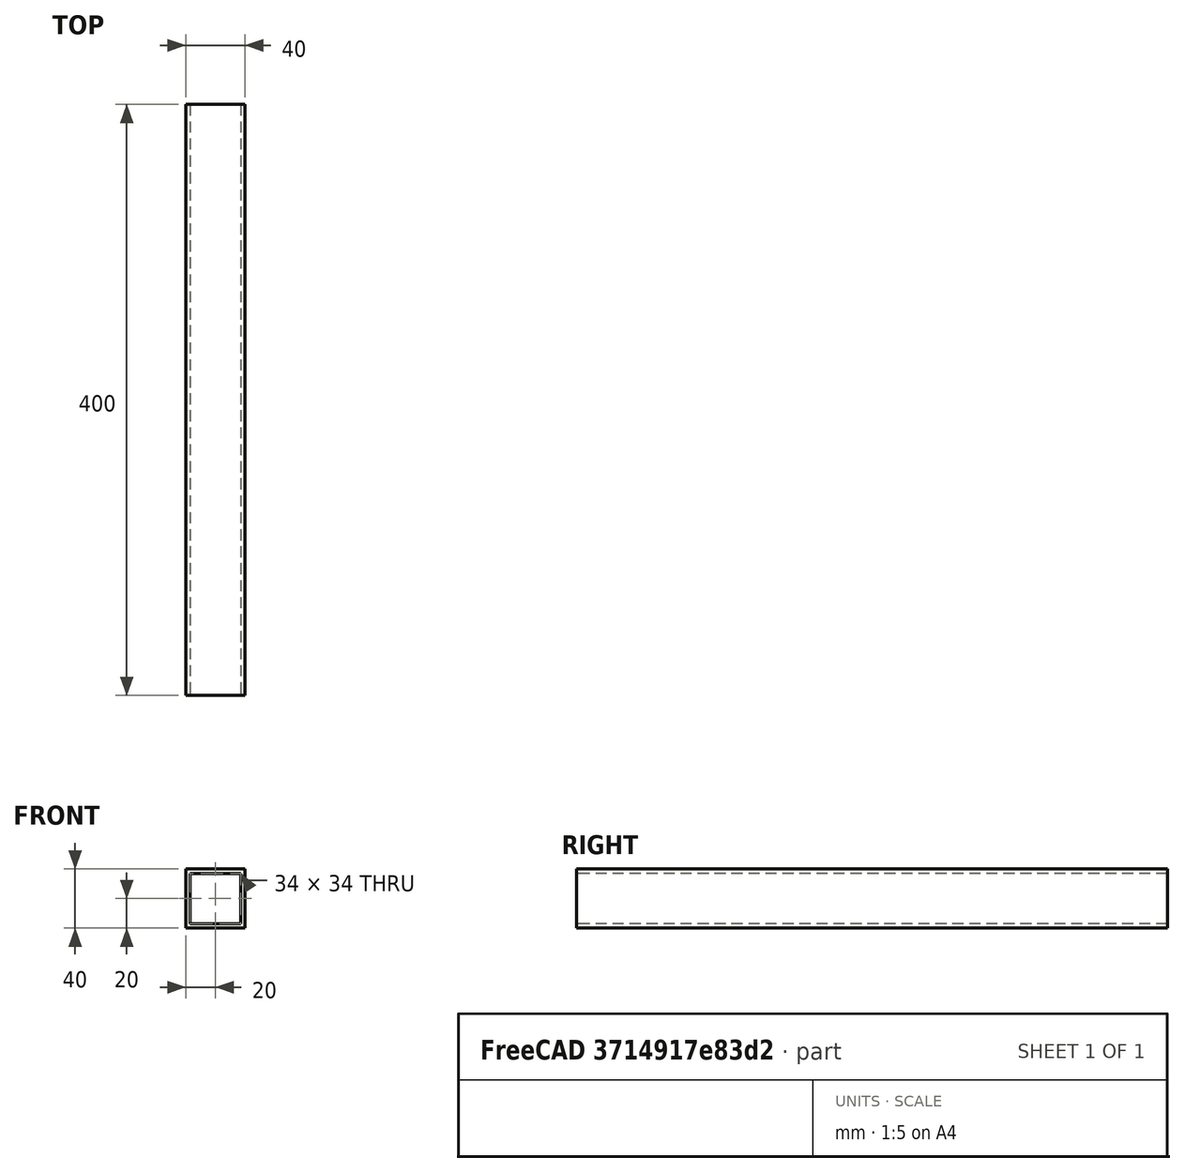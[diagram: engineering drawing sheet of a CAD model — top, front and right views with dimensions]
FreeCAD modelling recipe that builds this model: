
FCSTD DOCUMENT  (FreeCAD 0.20R29603 (Git))
Label: DaichselRohr
License: All rights reserved
LicenseURL: http://en.wikipedia.org/wiki/All_rights_reserved
objects: Sketcher::SketchObject×1, PartDesign::Pad×1, PartDesign::Body×1
note: 4 computed .brp shape members not serialized (recipe doc carries the construction recipe); baked Part::Feature solids carry a one-line shape summary decoded from their .brp

FEATURE [Sketcher::SketchObject] Sketch
  FullyConstrained = true
  MapMode = 5
  Placement = pos=(0,0,0) rot=(1,0,0;1.5708rad)
  Support = -> [XZ_Plane]
  sketch-geometry (10):
    g0: LineSegment StartX=-20 StartY=20 StartZ=0 EndX=-20 EndY=-20 EndZ=0
    g1: LineSegment StartX=-20 StartY=-20 StartZ=0 EndX=20 EndY=-20 EndZ=0
    g2: LineSegment StartX=20 StartY=-20 StartZ=0 EndX=20 EndY=20 EndZ=0
    g3: LineSegment StartX=20 StartY=20 StartZ=0 EndX=-20 EndY=20 EndZ=0
    g4: GeomPoint X=0 Y=0 Z=0
    g5: LineSegment StartX=-17 StartY=17 StartZ=0 EndX=-17 EndY=-17 EndZ=0
    g6: LineSegment StartX=-17 StartY=-17 StartZ=0 EndX=17 EndY=-17 EndZ=0
    g7: LineSegment StartX=17 StartY=-17 StartZ=0 EndX=17 EndY=17 EndZ=0
    g8: LineSegment StartX=17 StartY=17 StartZ=0 EndX=-17 EndY=17 EndZ=0
    g9: GeomPoint X=0 Y=0 Z=0
  constraints (24):
    c: Coincident(g0,g1)
    c: Coincident(g1,g2)
    c: Coincident(g2,g3)
    c: Coincident(g3,g0)
    c: Horizontal(g1)
    c: Horizontal(g3)
    c: Vertical(g0)
    c: Vertical(g2)
    c: Symmetric(g1,g0,g4)
    c: Coincident(g4,g-1)
    c: Coincident(g5,g6)
    c: Coincident(g6,g7)
    c: Coincident(g7,g8)
    c: Coincident(g8,g5)
    c: Horizontal(g6)
    c: Horizontal(g8)
    c: Vertical(g5)
    c: Vertical(g7)
    c: Symmetric(g6,g5,g9)
    c: Coincident(g9,g4)
    c: Distance(g3) = 40
    c: Distance(g2) = 40
    c: Distance(g6,g2) = 3
    c: Distance(g6,g1) = 3
FEATURE [PartDesign::Pad] Pad
  Direction = (0,-1,2e-16)
  Length = 400
  Length2 = 10
  Placement = pos=(0,0,0) rot=(1,0,0;1.5708rad)
  Profile = -> Sketch
  ReferenceAxis = -> Sketch [N_Axis]
  Type = 0
FEATURE [PartDesign::Body] Body
  Group = -> [Sketch,Pad]
  Origin = -> Origin
  Tip = -> Pad
